FCSTD DOCUMENT  (FreeCAD 0.20R29177 (Git))
Label: Cote2
License: All rights reserved
LicenseURL: http://en.wikipedia.org/wiki/All_rights_reserved
objects: TechDraw::DrawViewDimension×9, Sketcher::SketchObject×1, PartDesign::Body×1, TechDraw::DrawSVGTemplate×1, TechDraw::DrawProjGroupItem×1, TechDraw::DrawProjGroup×1, TechDraw::DrawPage×1
note: 2 computed .brp shape members not serialized (recipe doc carries the construction recipe); baked Part::Feature solids carry a one-line shape summary decoded from their .brp
EXTERNAL_REF file=DonneesBoitier.FCStd obj=Spreadsheet

FEATURE [Sketcher::SketchObject] Sketch
  FullyConstrained = true
  MapMode = 5
  Support = -> [XY_Plane001]
  expr: Constraints[0] = <<DonneesBoitier>>#<<Spreadsheet>>.xxAngle
  expr: Constraints[101] = <<DonneesBoitier>>#<<Spreadsheet>>.xxEpEcrou
  expr: Constraints[112] = 10mm
  expr: Constraints[114] = 10mm
  expr: Constraints[115] = 15mm
  expr: Constraints[123] = <<DonneesBoitier>>#<<Spreadsheet>>.xxDistEcrou
  expr: Constraints[155] = <<DonneesBoitier>>#<<Spreadsheet>>.xxLongVis
  expr: Constraints[156] = <<DonneesBoitier>>#<<Spreadsheet>>.xxLongVis
  expr: Constraints[1] = <<DonneesBoitier>>#<<Spreadsheet>>.xxHauteur - <<DonneesBoitier>>#<<Spreadsheet>>.xxFaEspaceHaut / 2 + <<DonneesBoitier>>#<<Spreadsheet>>.xxHautEncocheFemelle / 2
  expr: Constraints[27] = <<DonneesBoitier>>#<<Spreadsheet>>.xxLongEncoches
  expr: Constraints[39] = <<DonneesBoitier>>#<<Spreadsheet>>.xxLargEconche
  expr: Constraints[64] = <<DonneesBoitier>>#Spreadsheet.xxLargLatHaut
  expr: Constraints[65] = 25mm
  expr: Constraints[66] = <<DonneesBoitier>>#Spreadsheet.xxHauteurEncasEcran / 2 + <<DonneesBoitier>>#Spreadsheet.xxHautEncocheFemelle / 2 + <<DonneesBoitier>>#Spreadsheet.xxFaEspaceHaut / 2
  sketch-geometry (55):
    g0: LineSegment StartX=0 StartY=0 StartZ=0 EndX=-195.5 EndY=0 EndZ=0
    g1: LineSegment StartX=0 StartY=0 StartZ=0 EndX=6e-16 EndY=10 EndZ=0
    g2: LineSegment StartX=6e-16 StartY=10 StartZ=0 EndX=-8.66025 EndY=15 EndZ=0
    g3: LineSegment StartX=-8.66025 StartY=15 StartZ=0 EndX=-8.66025 EndY=10 EndZ=0
    g4: ArcOfCircle CenterX=0 CenterY=75.8274 CenterZ=0 NormalX=0 NormalY=0 NormalZ=1 AngleXU=0 Radius=66.3946 StartAngle=2.61481 EndAngle=4.58158
    g5: LineSegment StartX=-30.9735 StartY=164.968 StartZ=0 EndX=-34.4376 EndY=166.968 EndZ=0
    g6: LineSegment StartX=-38.4376 StartY=160.04 StartZ=0 EndX=-34.9735 EndY=158.04 EndZ=0
    g7: LineSegment StartX=-38.4376 StartY=160.04 StartZ=0 EndX=-37.7501 EndY=161.231 EndZ=0
    g8: LineSegment StartX=-37.7501 StartY=161.231 StartZ=0 EndX=-40.3482 EndY=162.731 EndZ=0
    g9: LineSegment StartX=-40.3482 StartY=162.731 StartZ=0 EndX=-37.7232 EndY=167.278 EndZ=0
    g10: LineSegment StartX=-37.7232 StartY=167.278 StartZ=0 EndX=-35.1251 EndY=165.778 EndZ=0
    g11: LineSegment StartX=-35.1251 StartY=165.778 StartZ=0 EndX=-34.4376 EndY=166.968 EndZ=0
    g12: LineSegment StartX=-79.4709 StartY=192.968 StartZ=0 EndX=-76.0068 EndY=190.968 EndZ=0
    g13: LineSegment StartX=-80.0068 StartY=184.04 StartZ=0 EndX=-83.4709 EndY=186.04 EndZ=0
    g14: LineSegment StartX=-80.0068 StartY=184.04 StartZ=0 EndX=-79.3193 EndY=185.231 EndZ=0
    g15: LineSegment StartX=-79.3193 StartY=185.231 StartZ=0 EndX=-75.8552 EndY=183.231 EndZ=0
    g16: LineSegment StartX=-75.8552 StartY=183.231 StartZ=0 EndX=-73.2302 EndY=187.778 EndZ=0
    g17: LineSegment StartX=-73.2302 StartY=187.778 StartZ=0 EndX=-76.6943 EndY=189.778 EndZ=0
    g18: LineSegment StartX=-76.6943 StartY=189.778 StartZ=0 EndX=-76.0068 EndY=190.968 EndZ=0
    g19: LineSegment StartX=-33.635 StartY=280.358 StartZ=0 EndX=-11.9844 EndY=267.858 EndZ=0
    g20: LineSegment StartX=1.00602 StartY=260.358 StartZ=0 EndX=22.6567 EndY=247.858 EndZ=0
    g21: LineSegment StartX=-11.9844 StartY=267.858 StartZ=0 EndX=-14.4844 EndY=263.528 EndZ=0
    g22: LineSegment StartX=-14.4844 StartY=263.528 StartZ=0 EndX=-1.49398 EndY=256.028 EndZ=0
    g23: LineSegment StartX=-1.49398 StartY=256.028 StartZ=0 EndX=1.00602 EndY=260.358 EndZ=0
    g24: LineSegment StartX=-28.6433 StartY=159.004 StartZ=0 EndX=-84.935 EndY=191.504 EndZ=0
    g25: LineSegment StartX=-39.8933 StartY=139.519 StartZ=0 EndX=-96.185 EndY=172.019 EndZ=0
    g26: LineSegment StartX=22.6567 StartY=247.858 StartZ=0 EndX=-13.6433 EndY=184.985 EndZ=0
    g27: LineSegment StartX=-43.6433 StartY=133.023 StartZ=0 EndX=-57.3933 EndY=109.208 EndZ=0
    g28: LineSegment StartX=-13.6433 StartY=184.985 StartZ=0 EndX=-9.31322 EndY=182.485 EndZ=0
    g29: LineSegment StartX=-9.31322 StartY=182.485 StartZ=0 EndX=-16.8132 EndY=169.495 EndZ=0
    g30: LineSegment StartX=-16.8132 StartY=169.495 StartZ=0 EndX=-21.1433 EndY=171.995 EndZ=0
    g31: LineSegment StartX=-36.1433 StartY=146.014 StartZ=0 EndX=-31.8132 EndY=143.514 EndZ=0
    g32: LineSegment StartX=-31.8132 StartY=143.514 StartZ=0 EndX=-39.3132 EndY=130.523 EndZ=0
    g33: LineSegment StartX=-39.3132 StartY=130.523 StartZ=0 EndX=-43.6433 EndY=133.023 EndZ=0
    g34: LineSegment StartX=-69.935 StartY=217.485 StartZ=0 EndX=-33.635 EndY=280.358 EndZ=0
    g35: LineSegment StartX=-195.5 StartY=0 StartZ=0 EndX=-99.935 EndY=165.523 EndZ=0
    g36: LineSegment StartX=-77.435 StartY=204.495 StartZ=0 EndX=-81.7651 EndY=206.995 EndZ=0
    g37: LineSegment StartX=-81.7651 StartY=206.995 StartZ=0 EndX=-74.2651 EndY=219.985 EndZ=0
    g38: LineSegment StartX=-74.2651 StartY=219.985 StartZ=0 EndX=-69.935 EndY=217.485 EndZ=0
    g39: LineSegment StartX=-99.935 StartY=165.523 StartZ=0 EndX=-104.265 EndY=168.023 EndZ=0
    g40: LineSegment StartX=-104.265 StartY=168.023 StartZ=0 EndX=-96.7651 EndY=181.014 EndZ=0
    g41: LineSegment StartX=-96.7651 StartY=181.014 StartZ=0 EndX=-92.435 EndY=178.514 EndZ=0
    g42: LineSegment StartX=-195.5 StartY=0 StartZ=0 EndX=0 EndY=338.616 EndZ=0
    g43: LineSegment StartX=-31.661 StartY=163.778 StartZ=0 EndX=-30.9735 EndY=164.968 EndZ=0
    g44: LineSegment StartX=-34.9735 StartY=158.04 StartZ=0 EndX=-34.286 EndY=159.231 EndZ=0
    g45: LineSegment StartX=-21.1433 StartY=171.995 StartZ=0 EndX=-27.3308 EndY=161.278 EndZ=0
    g46: LineSegment StartX=-29.9558 StartY=156.731 StartZ=0 EndX=-36.1433 EndY=146.014 EndZ=0
    g47: LineSegment StartX=-31.661 StartY=163.778 StartZ=0 EndX=-27.3308 EndY=161.278 EndZ=0
    g48: LineSegment StartX=-34.286 StartY=159.231 StartZ=0 EndX=-29.9558 EndY=156.731 EndZ=0
    g49: LineSegment StartX=-92.435 StartY=178.514 StartZ=0 EndX=-86.2475 EndY=189.231 EndZ=0
    g50: LineSegment StartX=-77.435 StartY=204.495 StartZ=0 EndX=-83.6225 EndY=193.778 EndZ=0
    g51: LineSegment StartX=-80.1584 StartY=191.778 StartZ=0 EndX=-79.4709 EndY=192.968 EndZ=0
    g52: LineSegment StartX=-83.4709 StartY=186.04 StartZ=0 EndX=-82.7834 EndY=187.231 EndZ=0
    g53: LineSegment StartX=-86.2475 StartY=189.231 StartZ=0 EndX=-82.7834 EndY=187.231 EndZ=0
    g54: LineSegment StartX=-83.6225 StartY=193.778 StartZ=0 EndX=-80.1584 EndY=191.778 EndZ=0
  constraints (157):
    c: Angle(g0,g35) = 1.0472
    c: Distance(g0,g19) = 323.73
    c: Tangent(g19,g20)
    c: Angle(g34,g19) = 1.5708
    c: Parallel(g34,g26)
    c: Parallel(g26,g29)
    c: Parallel(g29,g37)
    c: Parallel(g32,g40)
    c: Parallel(g21,g23)
    c: Coincident(g19,g34)
    c: Coincident(g21,g19)
    c: Coincident(g23,g20)
    c: Coincident(g20,g26)
    c: Coincident(g34,g38)
    c: Coincident(g37,g36)
    c: Coincident(g26,g28)
    c: Coincident(g29,g28)
    c: Coincident(g29,g30)
    c: Coincident(g30,g45)
    c: Parallel(g38,g19)
    c: Parallel(g36,g19)
    c: Parallel(g28,g30)
    c: Parallel(g30,g20)
    c: Parallel(g39,g41)
    c: Parallel(g41,g31)
    c: Parallel(g31,g33)
    c: Parallel(g33,g20)
    c: Distance(g26,g28) = 5
    c: Equal(g28,g38)
    c: Equal(g38,g36)
    c: Equal(g36,g30)
    c: Equal(g30,g23)
    c: Equal(g23,g21)
    c: Equal(g30,g31)
    c: Equal(g31,g33)
    c: Equal(g33,g39)
    c: Equal(g39,g41)
    c: Coincident(g22,g21)
    c: Coincident(g22,g23)
    c: Distance(g21,g22) = 15
    c: Equal(g22,g37)
    c: Equal(g37,g29)
    c: Equal(g29,g32)
    c: Equal(g32,g40)
    c: Coincident(g37,g38)
    c: Equal(g26,g34)
    c: PointOnObject(g0,g-1)
    c: Coincident(g0,g35)
    c: Coincident(g35,g39)
    c: Coincident(g40,g41)
    c: Coincident(g39,g40)
    c: Coincident(g42,g0)
    c: PointOnObject(g42,g-2)
    c: Angle(g0,g42) = 1.0472
    c: Distance(g0,g42) = 391
    c: Coincident(g0,g1)
    c: Coincident(g0,g-1)
    c: Symmetric(g41,g35,g25)
    c: Coincident(g46,g31)
    c: Coincident(g32,g31)
    c: Coincident(g32,g33)
    c: Coincident(g27,g33)
    c: Symmetric(g27,g46,g25)
    c: Coincident(g27,g4)
    c: Distance(g19,g20) = 65
    c: Distance(g19,g19) = 25
    c: Distance(g20,g24) = 102.6
    c: Symmetric(g8,g9,g24)
    c: Symmetric(g15,g16,g24)
    c: Coincident(g43,g5)
    c: Coincident(g10,g9)
    c: Coincident(g9,g8)
    c: Coincident(g44,g6)
    c: Parallel(g8,g10)
    c: Parallel(g10,g24)
    c: Coincident(g11,g10)
    c: Parallel(g11,g7)
    c: Parallel(g7,g9)
    c: Coincident(g5,g11)
    c: Parallel(g5,g6)
    c: Parallel(g6,g24)
    c: Coincident(g6,g7)
    c: Coincident(g8,g7)
    c: Distance(g5,g43) = 4
    c: Equal(g5,g6)
    c: Distance(g44,g43) = 8
    c: Symmetric(g43,g44,g24)
    c: Distance(g8,g9) = 5.25
    c: Symmetric(g41,g36,g24)
    c: Coincident(g16,g17)
    c: Coincident(g15,g16)
    c: Coincident(g13,g52)
    c: Coincident(g12,g51)
    c: Symmetric(g14,g17,g24)
    c: Symmetric(g12,g13,g24)
    c: Parallel(g24,g17)
    c: Parallel(g17,g12)
    c: Coincident(g18,g12)
    c: Coincident(g18,g17)
    c: Coincident(g15,g14)
    c: Coincident(g14,g13)
    c: Distance(g51,g12) = 4
    c: Distance(g52,g51) = 8
    c: Distance(g15,g16) = 5.25
    c: Parallel(g13,g24)
    c: PointOnObject(g24,g42)
    c: Parallel(g27,g35)
    c: PointOnObject(g4,g-2)
    c: Coincident(g4,g3)
    c: Coincident(g1,g2)
    c: Coincident(g2,g3)
    c: Distance(g2,g3) = 5
    c: Distance(g2,g1) = 10
    c: Angle(g-1,g1) = 1.5708
    c: Distance(g0,g1) = 10
    c: Distance(g2,g0) = 15
    c: Distance(g4,g27) = 27.5
    c: Parallel(g3,g1)
    c: Distance(g45,g24) = 15
    c: Parallel(g40,g43)
    c: Parallel(g40,g44)
    c: Equal(g7,g44)
    c: Parallel(g45,g32)
    c: Distance(g43,g45) = 5
    c: Coincident(g47,g43)
    c: Coincident(g47,g45)
    c: Parallel(g24,g47)
    c: Coincident(g48,g44)
    c: Coincident(g48,g46)
    c: Parallel(g48,g24)
    c: Equal(g48,g47)
    c: Symmetric(g44,g43,g24)
    c: Parallel(g25,g24)
    c: Equal(g25,g24)
    c: Coincident(g49,g41)
    c: PointOnObject(g49,g42)
    c: Coincident(g50,g36)
    c: PointOnObject(g50,g42)
    c: Symmetric(g49,g50,g24)
    c: Parallel(g51,g21)
    c: Parallel(g52,g21)
    c: Parallel(g52,g14)
    c: Equal(g52,g14)
    c: Equal(g18,g51)
    c: Parallel(g51,g18)
    c: PointOnObject(g54,g42)
    c: Coincident(g54,g51)
    c: Parallel(g53,g13)
    c: Parallel(g13,g54)
    c: Equal(g54,g53)
    c: Equal(g53,g12)
    c: Coincident(g53,g49)
    c: Coincident(g53,g52)
    c: Parallel(g46,g35)
    c: Parallel(g35,g34)
    c: Distance(g49,g15) = 12
    c: Distance(g8,g46) = 12
FEATURE [PartDesign::Body] Body001
  Group = -> [Sketch]
  Origin = -> Origin001
FEATURE [TechDraw::DrawSVGTemplate] Template
  EditableTexts = AUTHOR_NAME=Mike <owner>; DN=DN; DRAWING_TITLE=Coté; FC-DATE=14/08/2023; FC-REV=REV A; FC-SC=SCALE; FC-SH=X / Y; FC-SI=A4; FreeCAD_DRAWING=FreeCAD DRAWING; PN=PN
  Height = 297
  Orientation = 0
  Width = 210
FEATURE [TechDraw::DrawProjGroupItem] ProjItem  label="Front"
  CoarseView = false
  Direction = (0,0,1)
  Focus = 100
  HardHidden = false
  IsoCount = 0
  IsoHidden = false
  IsoVisible = false
  LockPosition = true
  Perspective = false
  Rotation = 0
  RotationVector = (1,0,0)
  Scale = 0.5
  ScaleType = 2
  SeamHidden = false
  SeamVisible = true
  SmoothHidden = false
  SmoothVisible = true
  Source = -> [Sketch]
  Type = 0
  X = 0
  XDirection = (1,0,0)
  Y = 0
FEATURE [TechDraw::DrawProjGroup] ProjGroup
  Anchor = -> ProjItem
  AutoDistribute = true
  LockPosition = false
  ProjectionType = 0
  Rotation = 0
  Scale = 0.5
  ScaleType = 1
  Source = -> [Sketch]
  Views = -> [ProjItem]
  X = 109.955
  Y = 166.333
  spacingX = 15
  spacingY = 15
FEATURE [TechDraw::DrawViewDimension] Dimension
  AngleOverride = false
  Arbitrary = false
  ArbitraryTolerances = false
  EqualTolerance = true
  ExtensionAngle = 0
  FormatSpec = %.2w
  FormatSpecOverTolerance = %+.2w
  FormatSpecUnderTolerance = %+.2w
  Inverted = false
  LineAngle = 0
  LockPosition = false
  MeasureType = 1
  OverTolerance = 0
  References2D = -> [ProjItem]
  Rotation = 0
  ScaleType = 0
  TheoreticalExact = false
  Type = 1
  UnderTolerance = 0
  X = -19.568
  Y = -73.472
FEATURE [TechDraw::DrawViewDimension] Dimension001
  AngleOverride = false
  Arbitrary = false
  ArbitraryTolerances = false
  EqualTolerance = true
  ExtensionAngle = 0
  FormatSpec = %.2w
  FormatSpecOverTolerance = %+.2w
  FormatSpecUnderTolerance = %+.2w
  Inverted = false
  LineAngle = 0
  LockPosition = false
  MeasureType = 1
  OverTolerance = 0
  References2D = -> [ProjItem]
  Rotation = 0
  ScaleType = 0
  TheoreticalExact = false
  Type = 2
  UnderTolerance = 0
  X = 50.1628
  Y = -73.9132
FEATURE [TechDraw::DrawViewDimension] Dimension002
  AngleOverride = false
  Arbitrary = false
  ArbitraryTolerances = false
  EqualTolerance = true
  ExtensionAngle = 0
  FormatSpec = %.2w
  FormatSpecOverTolerance = %+.2w
  FormatSpecUnderTolerance = %+.2w
  Inverted = false
  LineAngle = 0
  LockPosition = false
  MeasureType = 1
  OverTolerance = 0
  References2D = -> [ProjItem]
  Rotation = 0
  ScaleType = 0
  TheoreticalExact = false
  Type = 1
  UnderTolerance = 0
  X = 61.0994
  Y = -46.901
FEATURE [TechDraw::DrawViewDimension] Dimension003
  AngleOverride = false
  Arbitrary = false
  ArbitraryTolerances = false
  EqualTolerance = true
  ExtensionAngle = 0
  FormatSpec = %.2w
  FormatSpecOverTolerance = %+.2w
  FormatSpecUnderTolerance = %+.2w
  Inverted = false
  LineAngle = 0
  LockPosition = false
  MeasureType = 1
  OverTolerance = 0
  References2D = -> [ProjItem]
  Rotation = 0
  ScaleType = 0
  TheoreticalExact = false
  Type = 6
  UnderTolerance = 0
  X = -39.0378
  Y = -58.0219
FEATURE [TechDraw::DrawViewDimension] Dimension004
  AngleOverride = false
  Arbitrary = false
  ArbitraryTolerances = false
  EqualTolerance = true
  ExtensionAngle = 0
  FormatSpec = %.2w
  FormatSpecOverTolerance = %+.2w
  FormatSpecUnderTolerance = %+.2w
  Inverted = false
  LineAngle = 0
  LockPosition = false
  MeasureType = 1
  OverTolerance = 0
  References2D = -> [ProjItem]
  Rotation = 0
  ScaleType = 0
  TheoreticalExact = false
  Type = 0
  UnderTolerance = 0
  X = -36.4046
  Y = 12.8958
FEATURE [TechDraw::DrawViewDimension] Dimension005
  AngleOverride = false
  Arbitrary = false
  ArbitraryTolerances = false
  EqualTolerance = true
  ExtensionAngle = 0
  FormatSpec = %.2w
  FormatSpecOverTolerance = %+.2w
  FormatSpecUnderTolerance = %+.2w
  Inverted = false
  LineAngle = 0
  LockPosition = false
  MeasureType = 1
  OverTolerance = 0
  References2D = -> [ProjItem]
  Rotation = 0
  ScaleType = 0
  TheoreticalExact = false
  Type = 0
  UnderTolerance = 0
  X = 45.0866
  Y = 75.6305
FEATURE [TechDraw::DrawViewDimension] Dimension006
  AngleOverride = false
  Arbitrary = false
  ArbitraryTolerances = false
  EqualTolerance = true
  ExtensionAngle = 0
  FormatSpec = %.2w
  FormatSpecOverTolerance = %+.2w
  FormatSpecUnderTolerance = %+.2w
  Inverted = false
  LineAngle = 0
  LockPosition = false
  MeasureType = 1
  OverTolerance = 0
  References2D = -> [ProjItem]
  Rotation = 0
  ScaleType = 0
  TheoreticalExact = false
  Type = 0
  UnderTolerance = 0
  X = 45.3075
  Y = 15.5165
FEATURE [TechDraw::DrawViewDimension] Dimension007
  AngleOverride = false
  Arbitrary = false
  ArbitraryTolerances = false
  EqualTolerance = true
  ExtensionAngle = 0
  FormatSpec = %.2w
  FormatSpecOverTolerance = %+.2w
  FormatSpecUnderTolerance = %+.2w
  Inverted = false
  LineAngle = 0
  LockPosition = false
  MeasureType = 1
  OverTolerance = 0
  References2D = -> [ProjItem]
  Rotation = 0
  ScaleType = 0
  TheoreticalExact = false
  Type = 6
  UnderTolerance = 0
  X = 28.4922
  Y = 65.8401
FEATURE [TechDraw::DrawViewDimension] Dimension008
  AngleOverride = false
  Arbitrary = false
  ArbitraryTolerances = false
  EqualTolerance = true
  ExtensionAngle = 0
  FormatSpec = %.2w
  FormatSpecOverTolerance = %+.2w
  FormatSpecUnderTolerance = %+.2w
  Inverted = false
  LineAngle = 0
  LockPosition = false
  MeasureType = 1
  OverTolerance = 0
  References2D = -> [ProjItem]
  Rotation = 0
  ScaleType = 0
  TheoreticalExact = false
  Type = 2
  UnderTolerance = 0
  X = 6.92323
  Y = -51.3288
FEATURE [TechDraw::DrawPage] Page
  KeepUpdated = true
  NextBalloonIndex = 1
  ProjectionType = 0
  Template = -> Template
  Views = -> [ProjGroup,Dimension,Dimension001,Dimension002,Dimension003,Dimension004,Dimension005,Dimension006,Dimension007,Dimension008]
